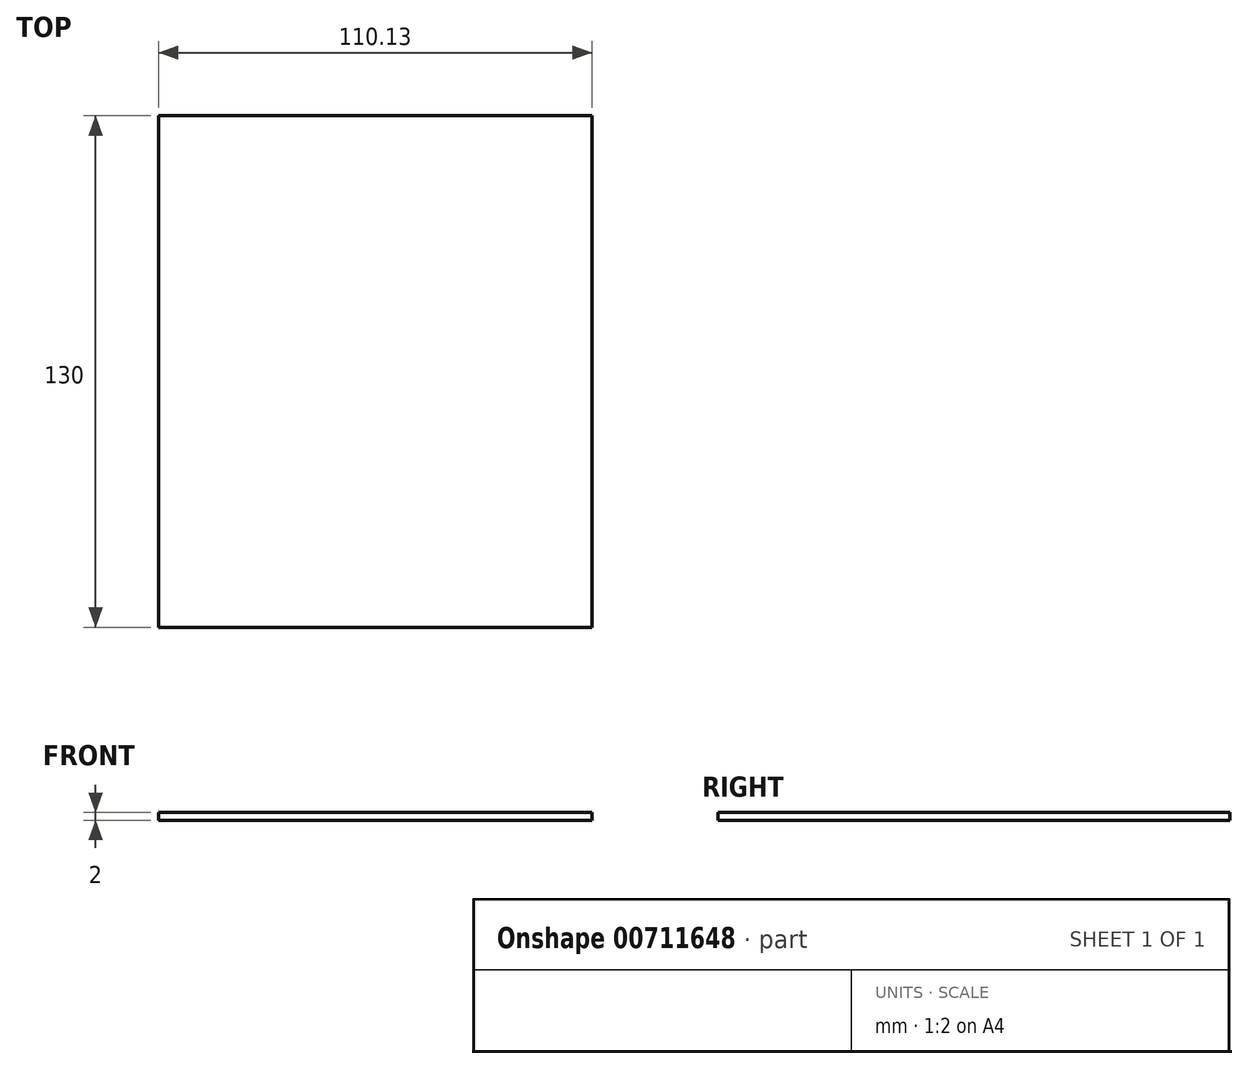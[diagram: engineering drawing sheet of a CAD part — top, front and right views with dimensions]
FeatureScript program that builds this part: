
annotation { "Feature Type Name" : "Feature", "Feature Type Description" : "" }
export const myFeature = defineFeature(function(context is Context, id is Id, definition is map)
    precondition{}
    {
        {
            var Q0;
            Q0=qCreatedBy(makeId("Top.planeOp"),FACE);
            var sketch = newSketch(context, id + "F0", { "sketchPlane" : qUnion([Q0])});
            skLineSegment(sketch, "E0.bottom", {"start": v(-55.54, 65.4) * mm, "end": v(54.59, 65.4) * mm});
            skLineSegment(sketch, "E0.top", {"start": v(-55.54, -64.6) * mm, "end": v(54.59, -64.6) * mm});
            skLineSegment(sketch, "E0.left", {"start": v(-55.54, 65.4) * mm, "end": v(-55.54, -64.6) * mm});
            skLineSegment(sketch, "E0.right", {"start": v(54.59, 65.4) * mm, "end": v(54.59, -64.6) * mm});
            skSolve(sketch);
        }
        {
            var Q0;
            Q0 = qSketchRegion(id + "F0", true);
            extrude(context, id + "F1", {"entities" : qUnion([Q0]), "depth" : 2 * mm, "offsetDistance" : 25 * mm});
        }
    });
